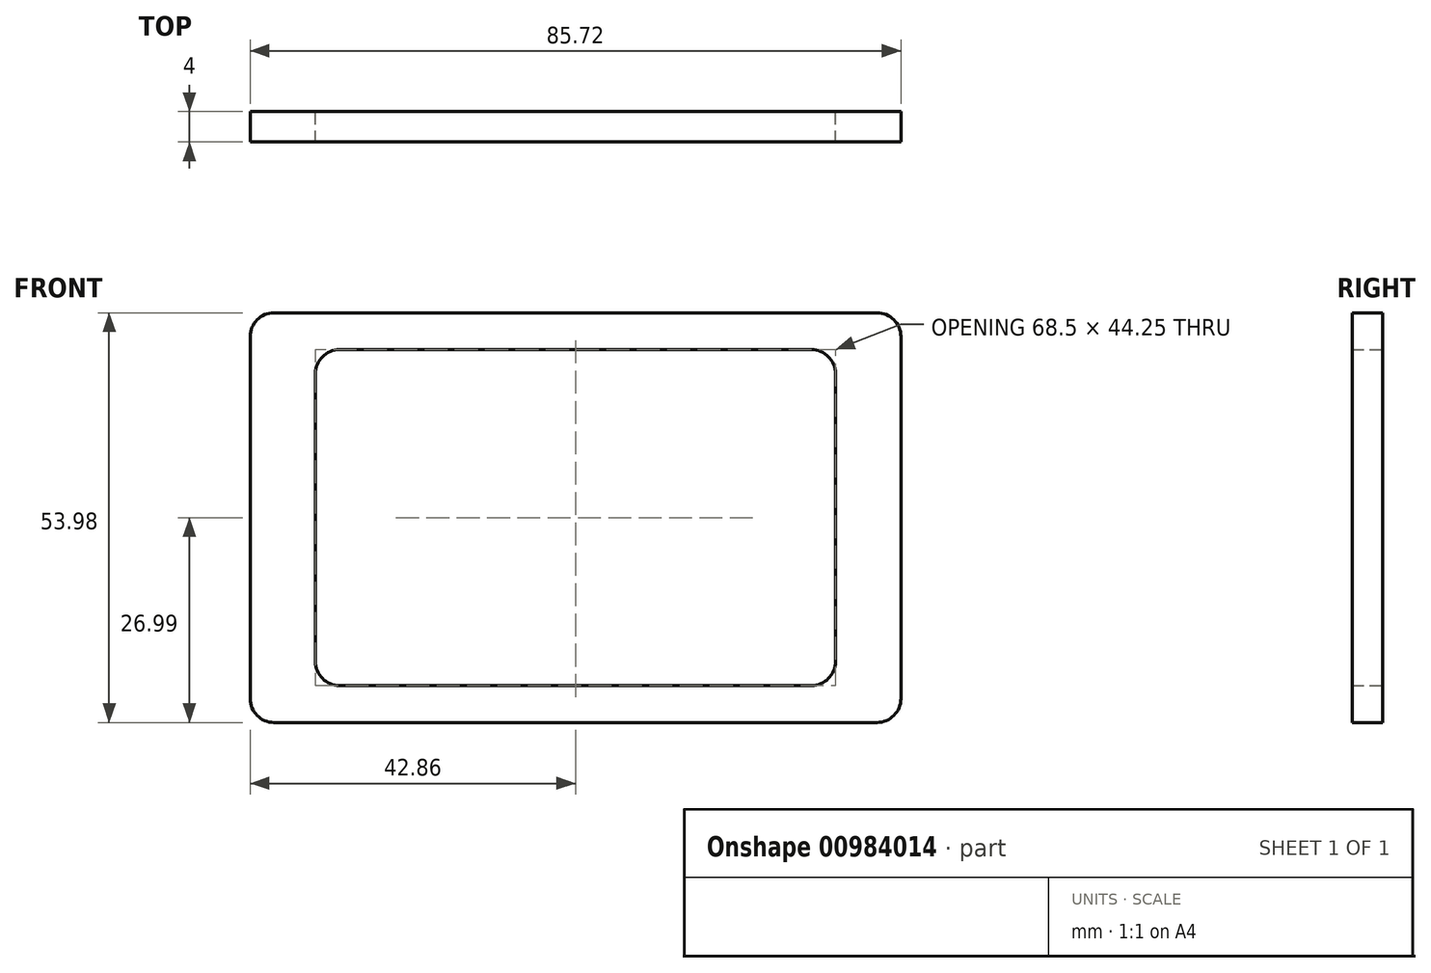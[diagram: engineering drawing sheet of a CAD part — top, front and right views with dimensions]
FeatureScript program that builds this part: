
annotation { "Feature Type Name" : "Feature", "Feature Type Description" : "" }
export const myFeature = defineFeature(function(context is Context, id is Id, definition is map)
    precondition{}
    {
        {
            var Q0;
            Q0=qCreatedBy(makeId("Front.planeOp"),FACE);
            var sketch = newSketch(context, id + "F0", { "sketchPlane" : qUnion([Q0])});
            skLineSegment(sketch, "E0.bottom", {"start": v(-39.71, 26.99) * mm, "end": v(39.71, 26.99) * mm});
            skLineSegment(sketch, "E0.top", {"start": v(-39.71, -26.99) * mm, "end": v(39.71, -26.99) * mm});
            skLineSegment(sketch, "E0.left", {"start": v(-42.86, 23.84) * mm, "end": v(-42.86, -23.84) * mm});
            skLineSegment(sketch, "E0.right", {"start": v(42.86, 23.84) * mm, "end": v(42.86, -23.84) * mm});
            skLineSegment(sketch, "E1", {"start": v(-42.86, 0) * mm, "end": v(0, 0) * mm});
            skLineSegment(sketch, "E2", {"start": v(0, 26.99) * mm, "end": v(0, 0) * mm});
            skPoint(sketch, "E3.visualSharp", {"position": v(-42.86, 26.99) * mm});
            skArc(sketch, "E3.filletArc", {"start": v(-39.71, 26.99) * mm, "mid": v(-41.94, 26.06) * mm, "end": v(-42.86, 23.84) * mm});
            skPoint(sketch, "E4.visualSharp", {"position": v(-42.86, -26.99) * mm});
            skArc(sketch, "E4.filletArc", {"start": v(-42.86, -23.84) * mm, "mid": v(-41.94, -26.06) * mm, "end": v(-39.71, -26.99) * mm});
            skPoint(sketch, "E5.visualSharp", {"position": v(42.86, -26.99) * mm});
            skArc(sketch, "E5.filletArc", {"start": v(39.71, -26.99) * mm, "mid": v(41.94, -26.06) * mm, "end": v(42.86, -23.84) * mm});
            skPoint(sketch, "E6.visualSharp", {"position": v(42.86, 26.99) * mm});
            skArc(sketch, "E6.filletArc", {"start": v(42.86, 23.84) * mm, "mid": v(41.94, 26.06) * mm, "end": v(39.71, 26.99) * mm});
            skLineSegment(sketch, "E7.bottom", {"start": v(-31.07, 22.12) * mm, "end": v(31.07, 22.12) * mm});
            skLineSegment(sketch, "E7.top", {"start": v(-31.07, -22.12) * mm, "end": v(31.07, -22.12) * mm});
            skLineSegment(sketch, "E7.left", {"start": v(-34.25, 18.95) * mm, "end": v(-34.25, -18.95) * mm});
            skLineSegment(sketch, "E7.right", {"start": v(34.25, 18.95) * mm, "end": v(34.25, -18.95) * mm});
            skLineSegment(sketch, "E8", {"start": v(0, 0) * mm, "end": v(0, 22.12) * mm});
            skLineSegment(sketch, "E9", {"start": v(-34.25, 0) * mm, "end": v(0, 0) * mm});
            skPoint(sketch, "E10.visualSharp", {"position": v(-34.25, 22.12) * mm});
            skArc(sketch, "E10.filletArc", {"start": v(-31.07, 22.12) * mm, "mid": v(-33.32, 21.2) * mm, "end": v(-34.25, 18.95) * mm});
            skPoint(sketch, "E11.visualSharp", {"position": v(-34.25, -22.12) * mm});
            skArc(sketch, "E11.filletArc", {"start": v(-34.25, -18.95) * mm, "mid": v(-33.32, -21.2) * mm, "end": v(-31.07, -22.13) * mm});
            skPoint(sketch, "E12.visualSharp", {"position": v(34.25, -22.12) * mm});
            skArc(sketch, "E12.filletArc", {"start": v(31.07, -22.12) * mm, "mid": v(33.32, -21.2) * mm, "end": v(34.25, -18.95) * mm});
            skPoint(sketch, "E13.visualSharp", {"position": v(34.25, 22.12) * mm});
            skArc(sketch, "E13.filletArc", {"start": v(34.25, 18.95) * mm, "mid": v(33.32, 21.2) * mm, "end": v(31.07, 22.13) * mm});
            skSolve(sketch);
        }
        {
            var Q0;
            Q0 = qSketchRegion(id + "F0", true);
            extrude(context, id + "F1", {"entities" : qUnion([Q0]), "depth" : 4 * mm, "offsetDistance" : 25.4 * mm});
        }
    });
